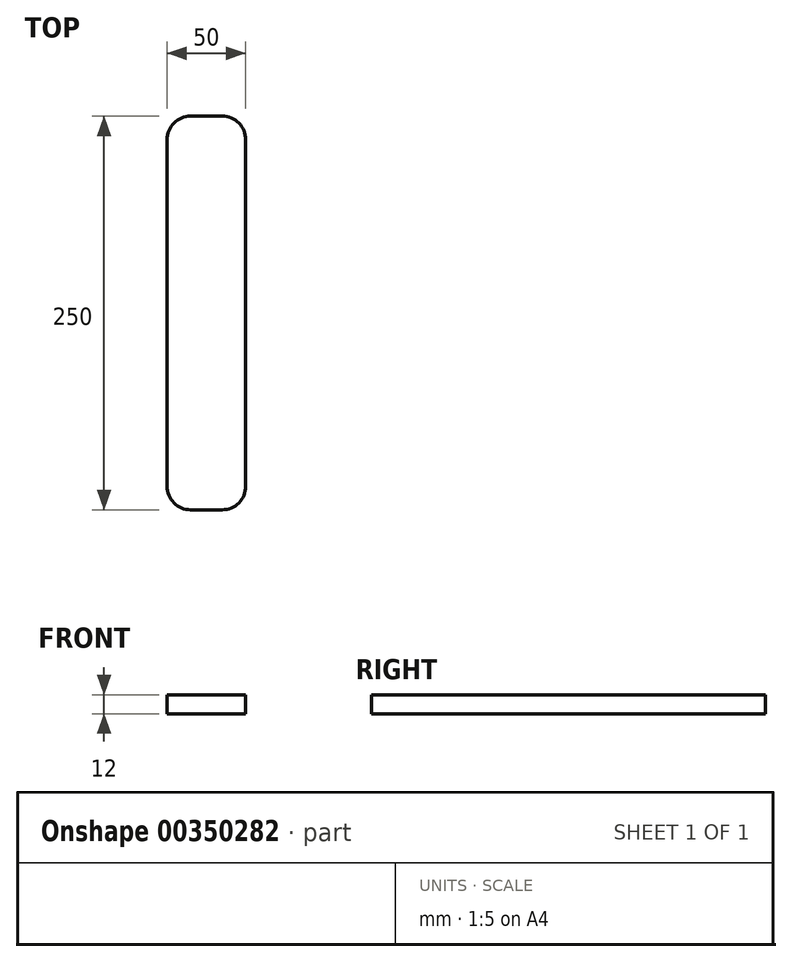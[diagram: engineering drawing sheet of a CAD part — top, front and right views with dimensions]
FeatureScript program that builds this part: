
annotation { "Feature Type Name" : "Feature", "Feature Type Description" : "" }
export const myFeature = defineFeature(function(context is Context, id is Id, definition is map)
    precondition{}
    {
        {
            var Q0;
            Q0=qCreatedBy(makeId("Top.planeOp"),FACE);
            var sketch = newSketch(context, id + "F0", { "sketchPlane" : qUnion([Q0])});
            skLineSegment(sketch, "E0.bottom", {"start": v(-10, 250) * mm, "end": v(10, 250) * mm});
            skLineSegment(sketch, "E0.top", {"start": v(-10, 0) * mm, "end": v(10, 0) * mm});
            skLineSegment(sketch, "E0.left", {"start": v(-25, 235) * mm, "end": v(-25, 15) * mm});
            skLineSegment(sketch, "E0.right", {"start": v(25, 235) * mm, "end": v(25, 15) * mm});
            skPoint(sketch, "E1.visualSharp", {"position": v(-25, 250) * mm});
            skArc(sketch, "E1.filletArc", {"start": v(-10, 250) * mm, "mid": v(-20.6, 245.6) * mm, "end": v(-25, 235) * mm});
            skPoint(sketch, "E2.visualSharp", {"position": v(25, 250) * mm});
            skArc(sketch, "E2.filletArc", {"start": v(25, 235) * mm, "mid": v(20.6, 245.6) * mm, "end": v(10, 250) * mm});
            skPoint(sketch, "E3.visualSharp", {"position": v(25, 0) * mm});
            skArc(sketch, "E3.filletArc", {"start": v(10, 0) * mm, "mid": v(20.6, 4.4) * mm, "end": v(25, 15) * mm});
            skPoint(sketch, "E4.visualSharp", {"position": v(-25, 0) * mm});
            skArc(sketch, "E4.filletArc", {"start": v(-25, 15) * mm, "mid": v(-20.6, 4.4) * mm, "end": v(-10, 0) * mm});
            skSolve(sketch);
        }
        {
            var Q0;
            Q0=makeQuery(id+"F0.imprint","IMPRINT",FACE,{"disambiguationData":[TD([[makeQuery(id+"F0.imprint","IMPRINT",EDGE,{"derivedFrom":sQuery(id+"F0.wireOp",EDGE,"E0.bottom")}),-1.0]])]});
            extrude(context, id + "F1", {"entities" : qUnion([Q0]), "depth" : 12 * mm});
        }
    });
